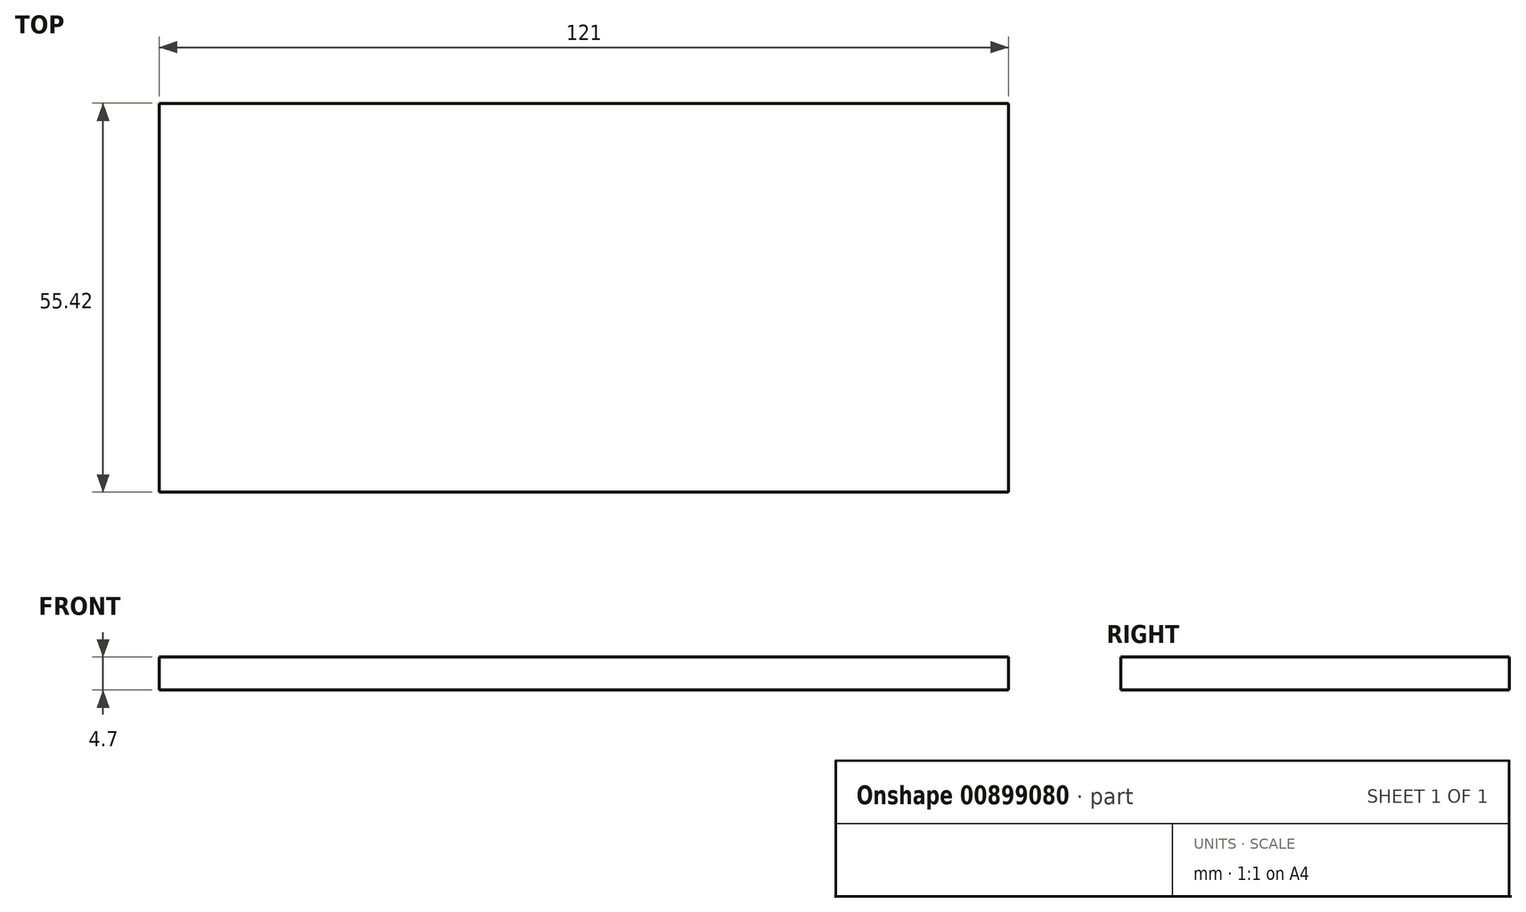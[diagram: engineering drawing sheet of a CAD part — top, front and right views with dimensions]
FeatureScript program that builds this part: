
annotation { "Feature Type Name" : "Feature", "Feature Type Description" : "" }
export const myFeature = defineFeature(function(context is Context, id is Id, definition is map)
    precondition{}
    {
        {
            var Q0;
            Q0=qCreatedBy(makeId("Top.planeOp"),FACE);
            var sketch = newSketch(context, id + "F0", { "sketchPlane" : qUnion([Q0])});
            skLineSegment(sketch, "E0.bottom", {"start": v(-60.5, 27.7) * mm, "end": v(60.5, 27.7) * mm});
            skLineSegment(sketch, "E0.top", {"start": v(-60.5, -27.7) * mm, "end": v(60.5, -27.7) * mm});
            skLineSegment(sketch, "E0.left", {"start": v(-60.5, 27.7) * mm, "end": v(-60.5, -27.7) * mm});
            skLineSegment(sketch, "E0.right", {"start": v(60.5, 27.7) * mm, "end": v(60.5, -27.7) * mm});
            skPoint(sketch, "E0.middle", {"position": v(0, 0) * mm});
            skSolve(sketch);
        }
        {
            var Q0;
            Q0=qSketchRegion(id+"F0",true);
            extrude(context, id + "F1", {"entities" : qUnion([Q0]), "depth" : 4.7 * mm, "offsetDistance" : 25 * mm});
        }
    });
